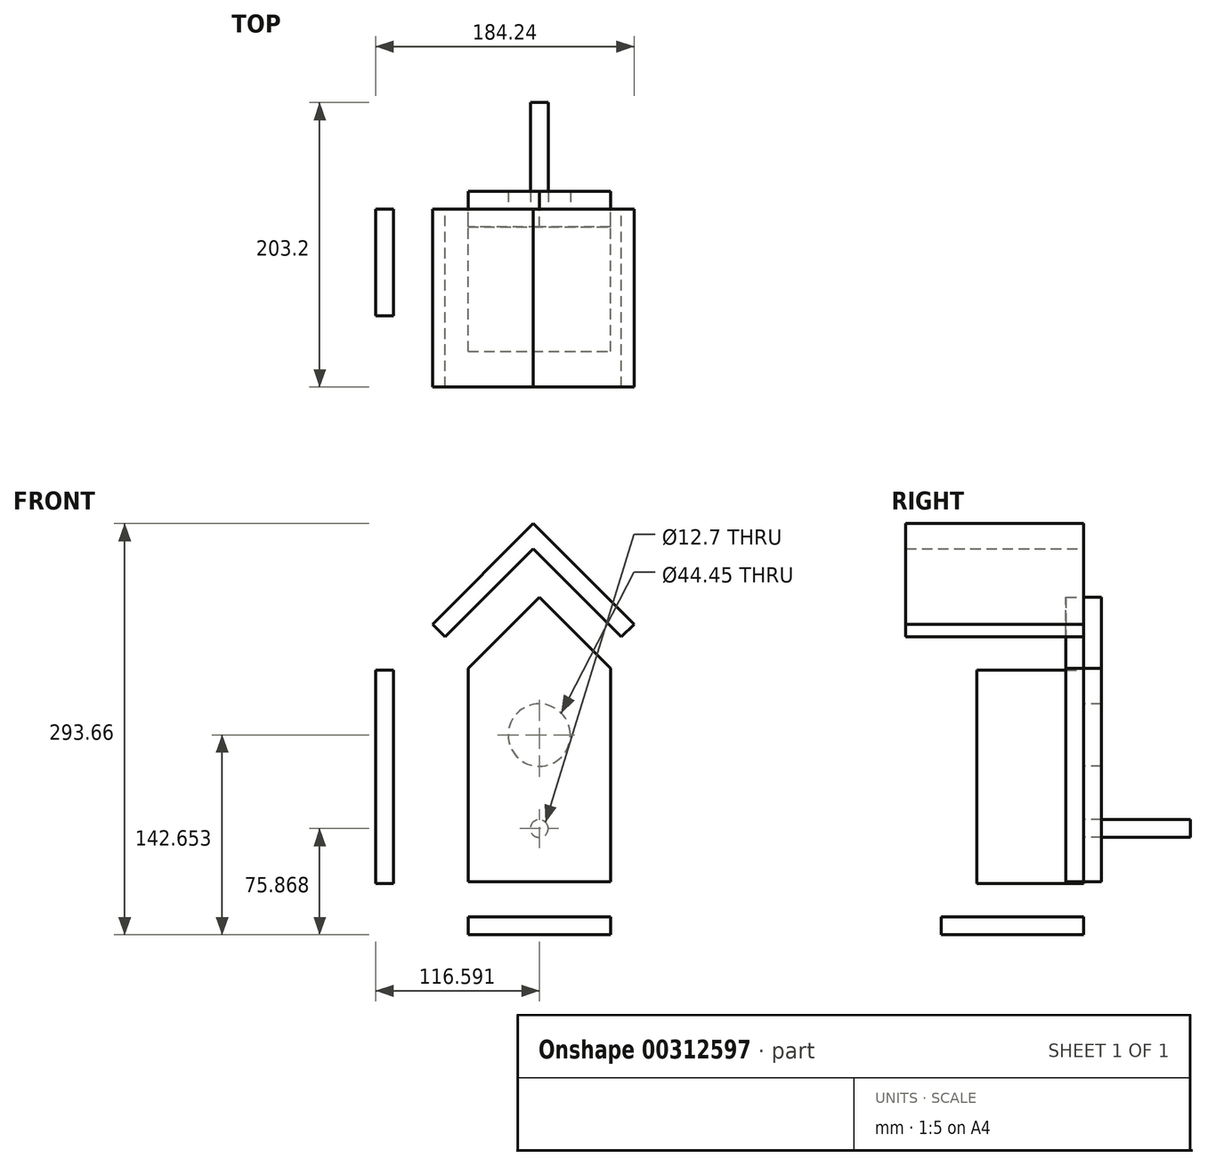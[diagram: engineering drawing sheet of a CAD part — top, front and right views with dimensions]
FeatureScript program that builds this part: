
annotation { "Feature Type Name" : "Feature", "Feature Type Description" : "" }
export const myFeature = defineFeature(function(context is Context, id is Id, definition is map)
    precondition{}
    {
        {
            var Q0;
            Q0=qCreatedBy(makeId("Front.planeOp"),FACE);
            var sketch = newSketch(context, id + "F0", { "sketchPlane" : qUnion([Q0])});
            skLineSegment(sketch, "E0.bottom", {"start": v(-124.3, 87.06) * mm, "end": v(-111.6, 87.06) * mm});
            skLineSegment(sketch, "E0.top", {"start": v(-124.3, -65.34) * mm, "end": v(-111.6, -65.34) * mm});
            skLineSegment(sketch, "E0.left", {"start": v(-124.3, 87.06) * mm, "end": v(-124.3, -65.34) * mm});
            skLineSegment(sketch, "E0.right", {"start": v(-111.6, 87.06) * mm, "end": v(-111.6, -65.34) * mm});
            skLineSegment(sketch, "E1.bottom", {"start": v(-58.5, -89.24) * mm, "end": v(43.1, -89.24) * mm});
            skLineSegment(sketch, "E1.top", {"start": v(-58.5, -101.94) * mm, "end": v(43.1, -101.94) * mm});
            skLineSegment(sketch, "E1.left", {"start": v(-58.5, -89.24) * mm, "end": v(-58.5, -101.94) * mm});
            skLineSegment(sketch, "E1.right", {"start": v(43.1, -89.24) * mm, "end": v(43.1, -101.94) * mm});
            skLineSegment(sketch, "E2.bottom", {"start": v(-58.5, 88.34) * mm, "end": v(43.1, 88.34) * mm});
            skLineSegment(sketch, "E2.top", {"start": v(-58.5, -64.06) * mm, "end": v(43.1, -64.06) * mm});
            skLineSegment(sketch, "E2.left", {"start": v(-58.5, 88.34) * mm, "end": v(-58.5, -64.06) * mm});
            skLineSegment(sketch, "E2.right", {"start": v(43.1, 88.34) * mm, "end": v(43.1, -64.06) * mm});
            skLineSegment(sketch, "E3", {"start": v(-7.7, 88.34) * mm, "end": v(-7.7, 139.14) * mm});
            skLineSegment(sketch, "E4", {"start": v(-7.7, 139.14) * mm, "end": v(-58.5, 88.34) * mm});
            skLineSegment(sketch, "E5", {"start": v(43.1, 88.34) * mm, "end": v(-7.7, 139.14) * mm});
            skLineSegment(sketch, "E6", {"start": v(-83.74, 119.88) * mm, "end": v(-74.76, 110.9) * mm});
            skLineSegment(sketch, "E7", {"start": v(-74.76, 110.9) * mm, "end": v(-11.9, 173.76) * mm});
            skLineSegment(sketch, "E8", {"start": v(-11.9, 173.76) * mm, "end": v(50.96, 110.9) * mm});
            skLineSegment(sketch, "E9", {"start": v(50.96, 110.9) * mm, "end": v(59.94, 119.88) * mm});
            skLineSegment(sketch, "E10", {"start": v(59.94, 119.88) * mm, "end": v(-11.9, 191.72) * mm});
            skLineSegment(sketch, "E11", {"start": v(-11.9, 191.72) * mm, "end": v(-83.74, 119.88) * mm});
            skCircle(sketch, "E12", {"center": v(-7.7, 40.71) * mm, "radius": 22.23 * mm});
            skCircle(sketch, "E13", {"center": v(-7.7, -26.07) * mm, "radius": 6.35 * mm});
            skSolve(sketch);
        }
        {
            var Q0;
            Q0=makeQuery(id+"F0.imprint","IMPRINT",FACE,{"disambiguationData":[TD([[makeQuery(id+"F0.imprint","IMPRINT",EDGE,{"derivedFrom":sQuery(id+"F0.wireOp",EDGE,"E1.bottom")}),-1.0]])]});
            extrude(context, id + "F1", {"entities" : qUnion([Q0]), "depth" : 101.6 * mm});
        }
        {
            var Q0;
            Q0=makeQuery(id+"F0.imprint","IMPRINT",FACE,{"disambiguationData":[TD([[makeQuery(id+"F0.imprint","IMPRINT",EDGE,{"derivedFrom":sQuery(id+"F0.wireOp",EDGE,"E0.bottom")}),-1.0]])]});
            extrude(context, id + "F2", {"entities" : qUnion([Q0]), "depth" : 76.2 * mm});
        }
        {
            var Q0;
            Q0=makeQuery(id+"F0.imprint","IMPRINT",FACE,{"disambiguationData":[TD([[makeQuery(id+"F0.imprint","IMPRINT",EDGE,{"derivedFrom":sQuery(id+"F0.wireOp",EDGE,"E2.top")}),1.0]])]});
            var Q1;
            {var subQ2=sQuery(id+"F0.wireOp",EDGE,"E3");Q1=makeQuery(id+"F0.imprint","IMPRINT",FACE,{"disambiguationData":[TD([[makeQuery(id+"F0.imprint","IMPRINT",EDGE,{"derivedFrom":subQ2}),1.0]])]});}
            var Q2;
            {var subQ2=sQuery(id+"F0.wireOp",EDGE,"E3");Q2=makeQuery(id+"F0.imprint","IMPRINT",FACE,{"disambiguationData":[TD([[makeQuery(id+"F0.imprint","IMPRINT",EDGE,{"derivedFrom":subQ2}),-1.0]])]});}
            var Q3;
            Q3=makeQuery(id+"F0.imprint","IMPRINT",FACE,{"disambiguationData":[TD([[makeQuery(id+"F0.imprint","IMPRINT",EDGE,{"derivedFrom":sQuery(id+"F0.wireOp",EDGE,"E12")}),1.0]])]});
            var Q4;
            Q4=makeQuery(id+"F0.imprint","IMPRINT",FACE,{"disambiguationData":[TD([[makeQuery(id+"F0.imprint","IMPRINT",EDGE,{"derivedFrom":sQuery(id+"F0.wireOp",EDGE,"E13")}),1.0]])]});
            extrude(context, id + "F3", {"entities" : qUnion([Q0, Q1, Q2, Q3, Q4]), "depth" : 12.7 * mm});
        }
        {
            var Q0;
            {var subQ2=sQuery(id+"F0.wireOp",EDGE,"E3");Q0=makeQuery(id+"F0.imprint","IMPRINT",FACE,{"disambiguationData":[TD([[makeQuery(id+"F0.imprint","IMPRINT",EDGE,{"derivedFrom":subQ2}),-1.0]])]});}
            var Q1;
            {var subQ2=sQuery(id+"F0.wireOp",EDGE,"E3");Q1=makeQuery(id+"F0.imprint","IMPRINT",FACE,{"disambiguationData":[TD([[makeQuery(id+"F0.imprint","IMPRINT",EDGE,{"derivedFrom":subQ2}),1.0]])]});}
            var Q2;
            Q2=makeQuery(id+"F0.imprint","IMPRINT",FACE,{"disambiguationData":[TD([[makeQuery(id+"F0.imprint","IMPRINT",EDGE,{"derivedFrom":sQuery(id+"F0.wireOp",EDGE,"E2.top")}),1.0]])]});
            extrude(context, id + "F4", {"entities" : qUnion([Q0, Q1, Q2]), "oppositeDirection" : true, "depth" : 12.7 * mm});
        }
        {
            var Q0;
            Q0=makeQuery(id+"F0.imprint","IMPRINT",FACE,{"disambiguationData":[TD([[makeQuery(id+"F0.imprint","IMPRINT",EDGE,{"derivedFrom":sQuery(id+"F0.wireOp",EDGE,"E6")}),1.0]])]});
            extrude(context, id + "F5", {"entities" : qUnion([Q0]), "depth" : 127 * mm});
        }
        {
            var Q0;
            Q0=makeQuery(id+"F0.imprint","IMPRINT",FACE,{"disambiguationData":[TD([[makeQuery(id+"F0.imprint","IMPRINT",EDGE,{"derivedFrom":sQuery(id+"F0.wireOp",EDGE,"E13")}),1.0]])]});
            extrude(context, id + "F6", {"entities" : qUnion([Q0]), "oppositeDirection" : true, "depth" : 76.2 * mm});
        }
    });
